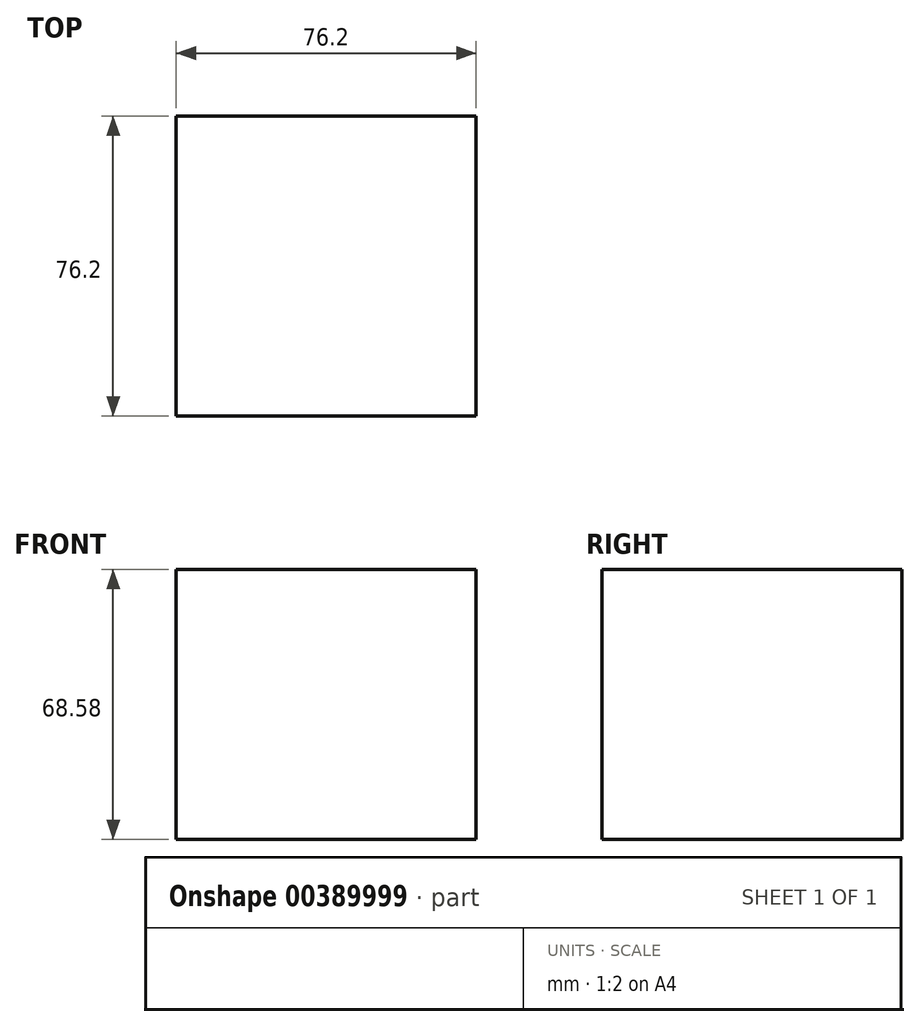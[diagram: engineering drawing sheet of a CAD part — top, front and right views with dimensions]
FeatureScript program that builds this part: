
annotation { "Feature Type Name" : "Feature", "Feature Type Description" : "" }
export const myFeature = defineFeature(function(context is Context, id is Id, definition is map)
    precondition{}
    {
        {
            var Q0;
            Q0=qCreatedBy(makeId("Top.planeOp"),FACE);
            var sketch = newSketch(context, id + "F0", { "sketchPlane" : qUnion([Q0])});
            skLineSegment(sketch, "E0.bottom", {"start": v(984.13, -433.05) * mm, "end": v(1060.33, -433.05) * mm});
            skLineSegment(sketch, "E0.top", {"start": v(984.13, -509.25) * mm, "end": v(1060.33, -509.25) * mm});
            skLineSegment(sketch, "E0.left", {"start": v(984.13, -433.05) * mm, "end": v(984.13, -509.25) * mm});
            skLineSegment(sketch, "E0.right", {"start": v(1060.33, -433.05) * mm, "end": v(1060.33, -509.25) * mm});
            skSolve(sketch);
        }
        {
            var Q0;
            Q0=makeQuery(id+"F0.imprint","IMPRINT",FACE,{"disambiguationData":[TD([[makeQuery(id+"F0.imprint","IMPRINT",EDGE,{"derivedFrom":sQuery(id+"F0.wireOp",EDGE,"E0.bottom")}),-1.0]])]});
            extrude(context, id + "F1", {"entities" : qUnion([Q0]), "depth" : 68.58 * mm});
        }
    });
